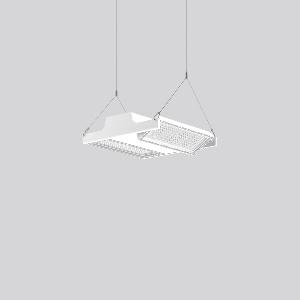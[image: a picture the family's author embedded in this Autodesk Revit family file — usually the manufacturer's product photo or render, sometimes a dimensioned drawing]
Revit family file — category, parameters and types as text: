
# Revit family: light_case_921681_002_1_76_54d2
name_source: partatom
category: Lighting Fixtures
units: mm (PartAtom-declared; Revit-internal decimal feet)

## family parameters
Cut with Voids When Loaded = No
Host = Face
Light Source = No
Part Type = Normal
Room Calculation Point = No
Round Connector Dimension = Use Diameter
Shared = No

## types (1)
- LIGHT CASE (1 x LED Modul 865, 8700 lm, 6500)
    Apparent Load = 117 VA
    CIE Flux Codes = 85 97 100 100 100
    Color Rendering = 80
    Color Temperature = 6500
    Default Elevation = 1800 mm
    Description = Series: LIGHT CASE
Flat highbay luminaire for chain or cable suspension with 2 LED modules that can be swivelled. Housing: die cast aluminium and sheet steel, powder-coated. Optimised thermal management thanks to special luminaire design. Self-cleaning heat sink for constant heat dissipation. Cover: plastic (polycarbonate, shockproof), with integrated four-row lens system. LED modules can be swivelled ± 30° for optimum illumination. Suitable for chain or steel cable suspension (to be provided on site). With 5-pin connection terminal (1.5 m). With integrated movement sensor and light sensor for daylight detection on request. Ball impact proof in accordance with DIN 18032-03 (except steel cable suspension). Luminaire with limited surface temperature in accordance with EN 60598-2-24 for use in environments in which a deposit of conductive dust on the luminaire can be expected. 
Colour: white
Length: 406 mm
Width: 397 mm
Height: 110 mm
Lamp: LED
Socket: without socket
Colour temperature: 6500K
Colour rendering index (CRI): 80
System power: 117 W
Rated luminous flux: 17400 lm
Luminous efficiency: 149 lm/W
Control gear: Converter, dimmable, DALI
Protection class: I
Type of protection: IP 65
    Height = 110 mm
    Lamp = 1 x LED Modul 865
    Lamp Light Flux = 8700 lm
    Lamp count = 1
    Length = 406 mm
    Lifetime = 50000 h
    Luminous efficacy = 149 lm/W
    Manufacturer = RZB
    ModVariant = No
    Model = 921681.002.1.76
    Mounting Place = Ceiling
    Mounting Type = Pendant
    Number of Poles = 1
    OnlyDefault = Yes
    Power Factor = 1
    Product Name = LIGHT CASE
    Product group = Pendant commercial luminaires
    ProductGroupID = 903
    Protection Class = Protection class I
    Protection Degree = IP 65
    RLX_Detail_Level = 1
    RLX_Emergency_Light_Flux = 0 lm
    RLX_Emergency_Type = 0
    RLX_Emergency_Type_DB = No
    RlxData = <blob elided: 25645 chars, md5=f0119418>
    Socket = socket
    Standby Power = 0 W
    System Light Flux = 17400 lm
    System Power = 117 W
    Type Comments = Product without accessories
    Type Image = 921517.002.76.jpg
    URL = http://relux.com
    VarID = ---
    Voltage = 230 V
    Voltage Range = 220-240 V
    Weight = 0.00 kg
    Width = 397 mm

## geometry (parser evidence)
native form markers: Blend x4, Sweep x17
no freeform markers — native parametric forms only
